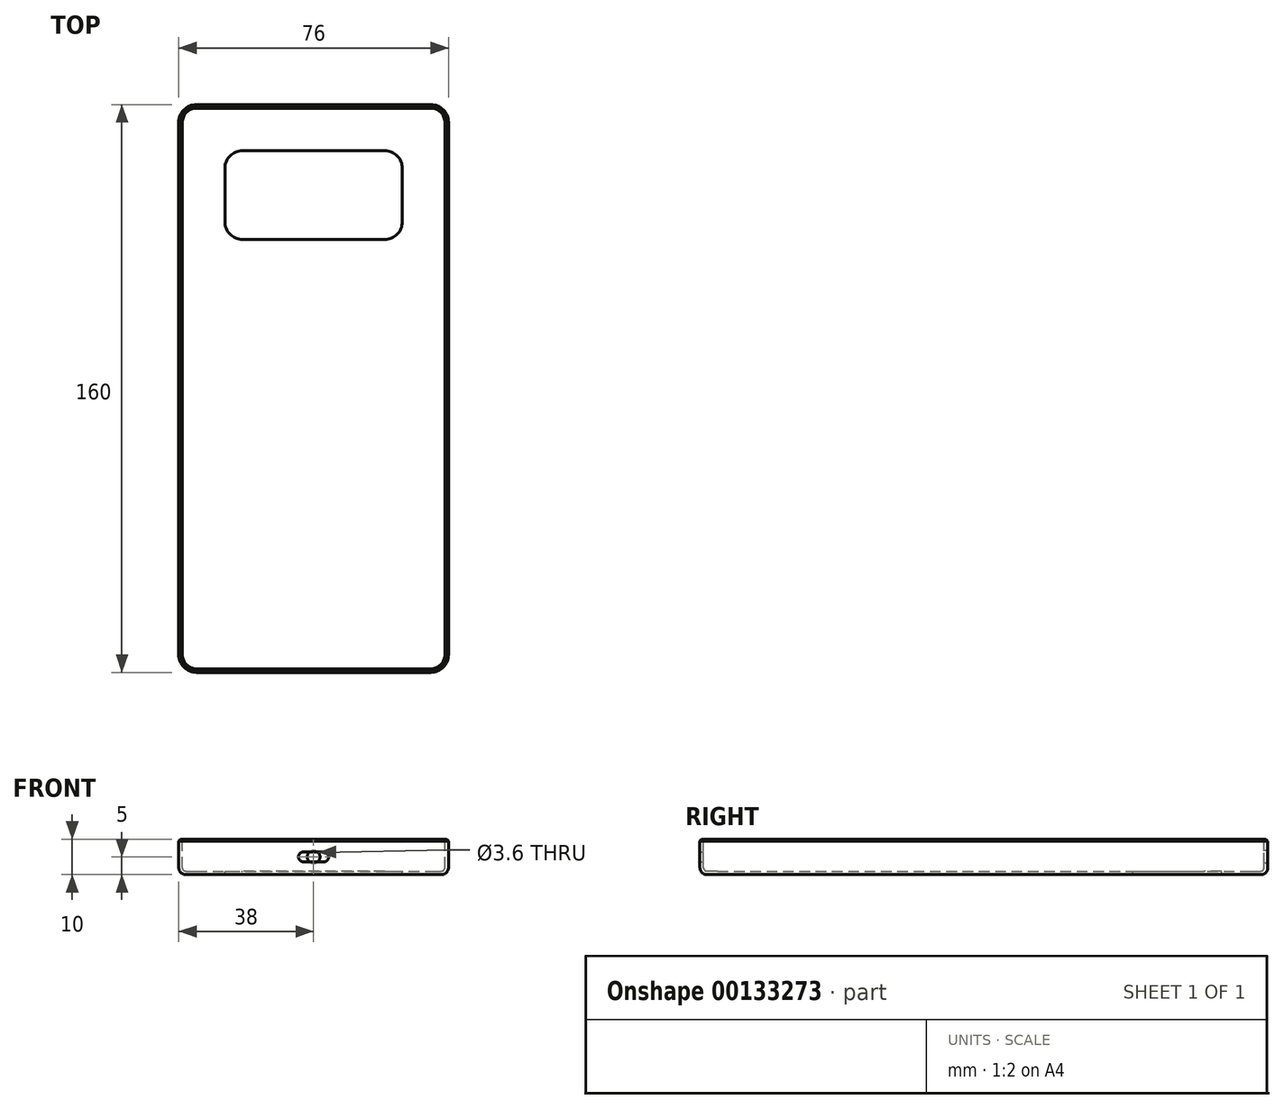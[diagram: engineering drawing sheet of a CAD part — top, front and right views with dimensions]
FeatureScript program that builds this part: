
annotation { "Feature Type Name" : "Feature", "Feature Type Description" : "" }
export const myFeature = defineFeature(function(context is Context, id is Id, definition is map)
    precondition{}
    {
        {
            var Q0;
            Q0=qCreatedBy(makeId("Top.planeOp"),FACE);
            var sketch = newSketch(context, id + "F0", { "sketchPlane" : qUnion([Q0])});
            skLineSegment(sketch, "E0.bottom", {"start": v(-33, 80) * mm, "end": v(33, 80) * mm});
            skLineSegment(sketch, "E0.top", {"start": v(-33, -80) * mm, "end": v(33, -80) * mm});
            skLineSegment(sketch, "E0.left", {"start": v(-38, 75) * mm, "end": v(-38, -75) * mm});
            skLineSegment(sketch, "E0.right", {"start": v(38, 75) * mm, "end": v(38, -75) * mm});
            skPoint(sketch, "E1.visualSharp", {"position": v(-38, 80) * mm});
            skArc(sketch, "E1.filletArc", {"start": v(-33, 80) * mm, "mid": v(-36.54, 78.54) * mm, "end": v(-38, 75) * mm});
            skPoint(sketch, "E2.visualSharp", {"position": v(38, 80) * mm});
            skArc(sketch, "E2.filletArc", {"start": v(38, 75) * mm, "mid": v(36.54, 78.54) * mm, "end": v(33, 80) * mm});
            skPoint(sketch, "E3.visualSharp", {"position": v(38, -80) * mm});
            skArc(sketch, "E3.filletArc", {"start": v(33, -80) * mm, "mid": v(36.54, -78.54) * mm, "end": v(38, -75) * mm});
            skPoint(sketch, "E4.visualSharp", {"position": v(-38, -80) * mm});
            skArc(sketch, "E4.filletArc", {"start": v(-38, -75) * mm, "mid": v(-36.54, -78.54) * mm, "end": v(-33, -80) * mm});
            skSolve(sketch);
        }
        {
            var Q0;
            Q0=makeQuery(id+"F0.imprint","IMPRINT",FACE,{"disambiguationData":[TD([[makeQuery(id+"F0.imprint","IMPRINT",EDGE,{"derivedFrom":sQuery(id+"F0.wireOp",EDGE,"E0.bottom")}),-1.0]])]});
            extrude(context, id + "F1", {"entities" : qUnion([Q0]), "oppositeDirection" : true, "depth" : 10 * mm});
        }
        {
            var Q0;
            Q0=makeQuery(id+"F1.opExtrude","CAP_EDGE",EDGE,{"disambiguationData":[OSD([sQuery(id+"F0.wireOp",EDGE,"E0.bottom")])],"isStart":false});
            fillet(context, id + "F2", {"entities" : qUnion([Q0]), "radius" : 2 * mm, "tangentPropagation" : true, "allowEdgeOverflow" : false});
        }
        {
            var Q0;
            Q0=makeQuery(id+"F1.opExtrude","CAP_FACE",FACE,{"disambiguationData":[OSD([sQuery(id+"F0.wireOp",EDGE,"E0.bottom"),sQuery(id+"F0.wireOp",EDGE,"E0.top"),sQuery(id+"F0.wireOp",EDGE,"E0.left"),sQuery(id+"F0.wireOp",EDGE,"E0.right"),sQuery(id+"F0.wireOp",EDGE,"E1.filletArc"),sQuery(id+"F0.wireOp",EDGE,"E2.filletArc"),sQuery(id+"F0.wireOp",EDGE,"E3.filletArc"),sQuery(id+"F0.wireOp",EDGE,"E4.filletArc")])],"isStart":true});
            shell(context, id + "F3", {"entities" : qUnion([Q0]), "thickness" : 1 * mm});
        }
        {
            var Q0;
            Q0=makeQuery(id+"F1.opExtrude","CAP_EDGE",EDGE,{"disambiguationData":[OSD([sQuery(id+"F0.wireOp",EDGE,"E4.filletArc")])],"isStart":true});
            chamfer(context, id + "F4", {"entities" : qUnion([Q0]), "width" : 0.5 * mm, "tangentPropagation" : true});
        }
        {
            var Q0;
            Q0=qCreatedBy(makeId("Top.planeOp"),FACE);
            var sketch = newSketch(context, id + "F5", { "sketchPlane" : qUnion([Q0])});
            skLineSegment(sketch, "E5.bottom", {"start": v(20, 42) * mm, "end": v(-20, 42) * mm});
            skLineSegment(sketch, "E5.top", {"start": v(20, 67) * mm, "end": v(-20, 67) * mm});
            skLineSegment(sketch, "E5.left", {"start": v(25, 47) * mm, "end": v(25, 62) * mm});
            skLineSegment(sketch, "E5.right", {"start": v(-25, 47) * mm, "end": v(-25, 62) * mm});
            skPoint(sketch, "E5.middle", {"position": v(0, 54.5) * mm});
            skPoint(sketch, "E6.visualSharp", {"position": v(-25, 67) * mm});
            skArc(sketch, "E6.filletArc", {"start": v(-20, 67) * mm, "mid": v(-23.54, 65.54) * mm, "end": v(-25, 62) * mm});
            skPoint(sketch, "E7.visualSharp", {"position": v(25, 67) * mm});
            skArc(sketch, "E7.filletArc", {"start": v(25, 62) * mm, "mid": v(23.54, 65.54) * mm, "end": v(20, 67) * mm});
            skPoint(sketch, "E8.visualSharp", {"position": v(25, 42) * mm});
            skArc(sketch, "E8.filletArc", {"start": v(20, 42) * mm, "mid": v(23.54, 43.46) * mm, "end": v(25, 47) * mm});
            skPoint(sketch, "E9.visualSharp", {"position": v(-25, 42) * mm});
            skArc(sketch, "E9.filletArc", {"start": v(-25, 47) * mm, "mid": v(-23.54, 43.46) * mm, "end": v(-20, 42) * mm});
            skLineSegment(sketch, "E10.bottom", {"start": v(38, 80) * mm, "end": v(-38, 80) * mm, "construction": true});
            skLineSegment(sketch, "E10.top", {"start": v(38, -80) * mm, "end": v(-38, -80) * mm, "construction": true});
            skLineSegment(sketch, "E10.left", {"start": v(38, 80) * mm, "end": v(38, -80) * mm, "construction": true});
            skLineSegment(sketch, "E10.right", {"start": v(-38, 80) * mm, "end": v(-38, -80) * mm, "construction": true});
            skPoint(sketch, "E10.middle", {"position": v(0, 0) * mm});
            skLineSegment(sketch, "E11", {"start": v(25, 67) * mm, "end": v(38, 80) * mm, "construction": true});
            skSolve(sketch);
        }
        {
            var Q0;
            Q0=makeQuery(id+"F5.imprint","IMPRINT",FACE,{"disambiguationData":[TD([[makeQuery(id+"F5.imprint","IMPRINT",EDGE,{"derivedFrom":sQuery(id+"F5.wireOp",EDGE,"E5.bottom")}),-1.0]])]});
            var Q1;
            Q1=sQuery(id+"F5.wireOp",EDGE,"E11");
            var Q2;
            Q2=sQuery(id+"F5.wireOp",EDGE,"E10.bottom");
            var Q3;
            Q3=sQuery(id+"F5.wireOp",EDGE,"E10.right");
            var Q4;
            Q4=sQuery(id+"F5.wireOp",EDGE,"E10.left");
            var Q5;
            Q5=sQuery(id+"F5.wireOp",EDGE,"E10.top");
            extrude(context, id + "F6", {"entities" : qUnion([Q0]), "operationType" : NewBodyOperationType.REMOVE, "surfaceEntities" : qUnion([Q1, Q2, Q3, Q4, Q5]), "endBound" : BoundingType.THROUGH_ALL, "oppositeDirection" : true, "depth" : 25 * mm});
        }
        {
            var Q0;
            Q0=qCreatedBy(makeId("Front.planeOp"),FACE);
            var sketch = newSketch(context, id + "F7", { "sketchPlane" : qUnion([Q0])});
            skArc(sketch, "E12", {"start": v(-2.85, -3.6) * mm, "mid": v(-4.25, -5) * mm, "end": v(-2.85, -6.4) * mm});
            skArc(sketch, "E13", {"start": v(2.85, -6.4) * mm, "mid": v(4.25, -5) * mm, "end": v(2.85, -3.6) * mm});
            skLineSegment(sketch, "E14", {"start": v(-2.85, -3.6) * mm, "end": v(2.85, -3.6) * mm});
            skLineSegment(sketch, "E15", {"start": v(2.85, -6.4) * mm, "end": v(-2.85, -6.4) * mm});
            skSolve(sketch);
        }
        {
            var Q0;
            Q0 = qSketchRegion(id + "F7", true);
            extrude(context, id + "F8", {"entities" : qUnion([Q0]), "operationType" : NewBodyOperationType.REMOVE, "endBound" : BoundingType.THROUGH_ALL, "depth" : 25 * mm});
        }
        {
            var Q0;
            Q0=qCreatedBy(makeId("Front.planeOp"),FACE);
            var sketch = newSketch(context, id + "F9", { "sketchPlane" : qUnion([Q0])});
            skCircle(sketch, "E16", {"center": v(0, -5) * mm, "radius": 1.8 * mm});
            skSolve(sketch);
        }
        {
            var Q0;
            Q0 = qSketchRegion(id + "F9", true);
            extrude(context, id + "F10", {"entities" : qUnion([Q0]), "operationType" : NewBodyOperationType.REMOVE, "endBound" : BoundingType.THROUGH_ALL, "oppositeDirection" : true, "depth" : 25 * mm});
        }
        {
            var Q0;
            {var subQ0=sQuery(id+"F0.wireOp",EDGE,"E0.bottom");Q0=makeQuery(id+"F3.opShell","OFFSET_EDGE",EDGE,{"disambiguationData":[OSD([subQ0]),TDD([makeQuery(id+"F1.opExtrude","CAP_EDGE",EDGE,{"disambiguationData":[OSD([subQ0])],"isStart":true})])]});}
            var Q1;
            Q1=makeQuery(id+"F6.boolean.opBoolean","INTERSECT",EDGE,{"derivedFrom":[makeQuery(id+"F1.opExtrude","CAP_FACE",FACE,{"disambiguationData":[OSD([sQuery(id+"F0.wireOp",EDGE,"E0.bottom"),sQuery(id+"F0.wireOp",EDGE,"E0.top"),sQuery(id+"F0.wireOp",EDGE,"E0.left"),sQuery(id+"F0.wireOp",EDGE,"E0.right"),sQuery(id+"F0.wireOp",EDGE,"E1.filletArc"),sQuery(id+"F0.wireOp",EDGE,"E2.filletArc"),sQuery(id+"F0.wireOp",EDGE,"E3.filletArc"),sQuery(id+"F0.wireOp",EDGE,"E4.filletArc")])],"isStart":false}),makeQuery(id+"F6.opExtrude","SWEPT_FACE",FACE,{"disambiguationData":[OSD([sQuery(id+"F5.wireOp",EDGE,"E5.top")])]})]});
            var Q2;
            Q2=makeQuery(id+"F8.boolean.opBoolean","INTERSECT",EDGE,{"derivedFrom":[makeQuery(id+"F1.opExtrude","SWEPT_FACE",FACE,{"disambiguationData":[OSD([sQuery(id+"F0.wireOp",EDGE,"E0.top")])]}),makeQuery(id+"F8.opExtrude","SWEPT_FACE",FACE,{"disambiguationData":[OSD([sQuery(id+"F7.wireOp",EDGE,"E15")])]})]});
            var Q3;
            Q3=makeQuery(id+"F10.boolean.opBoolean","INTERSECT",EDGE,{"derivedFrom":[makeQuery(id+"F1.opExtrude","SWEPT_FACE",FACE,{"disambiguationData":[OSD([sQuery(id+"F0.wireOp",EDGE,"E0.bottom")])]}),makeQuery(id+"F10.opExtrude","SWEPT_FACE",FACE,{"disambiguationData":[OSD([sQuery(id+"F9.wireOp",EDGE,"E16")])]})]});
            fillet(context, id + "F11", {"entities" : qUnion([Q0, Q1, Q2, Q3]), "radius" : 0.2 * mm, "tangentPropagation" : true, "allowEdgeOverflow" : false});
        }
    });
